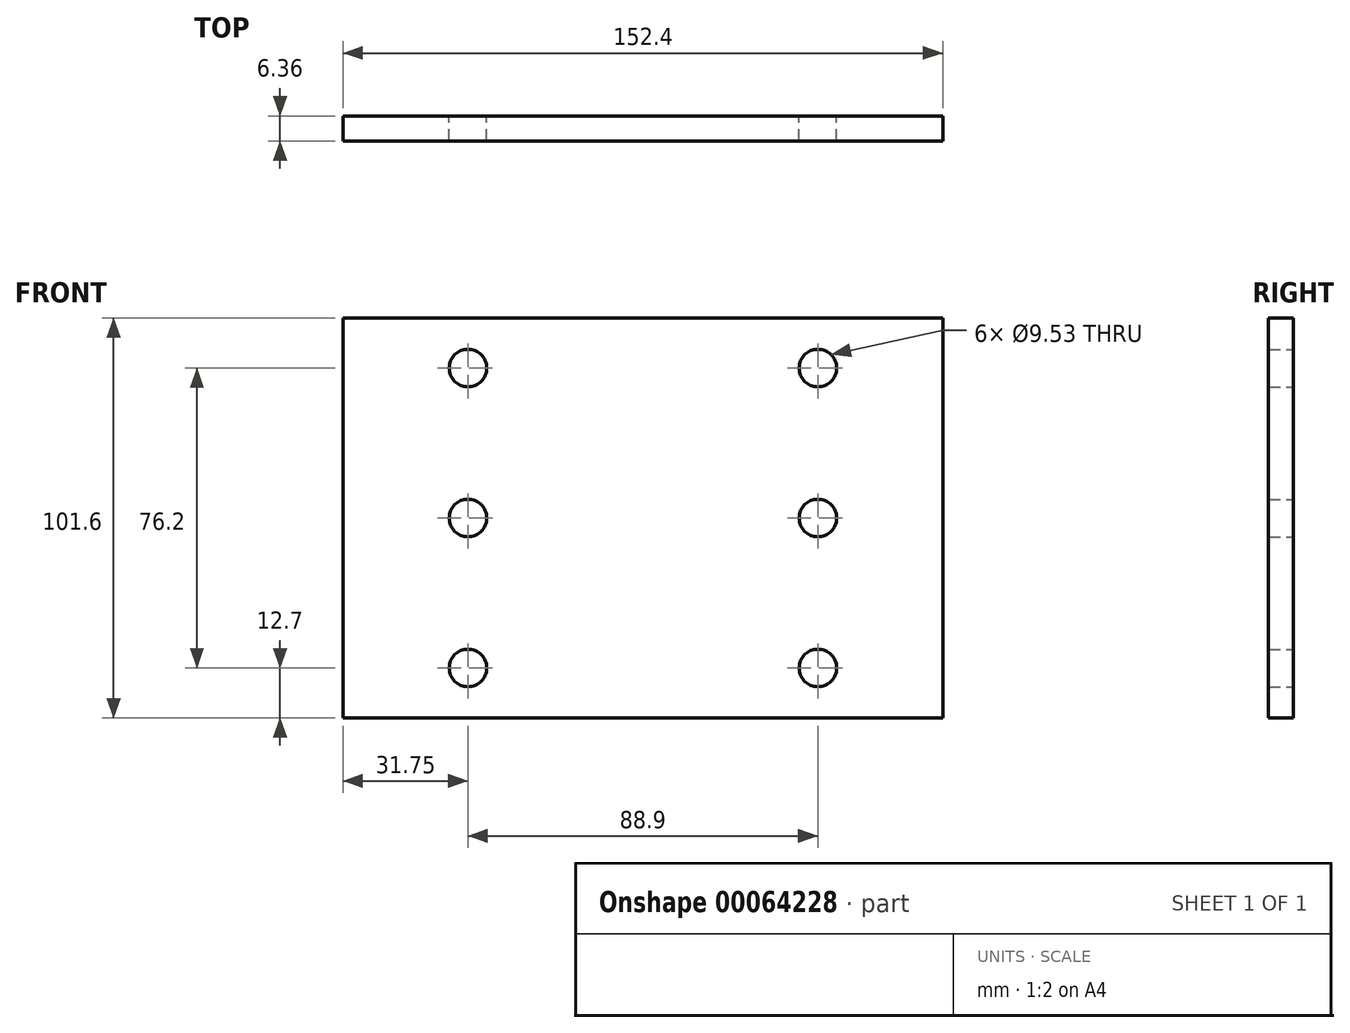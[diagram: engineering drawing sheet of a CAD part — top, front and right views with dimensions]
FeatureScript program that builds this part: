
annotation { "Feature Type Name" : "Feature", "Feature Type Description" : "" }
export const myFeature = defineFeature(function(context is Context, id is Id, definition is map)
    precondition{}
    {
        {
            var Q0;
            Q0=qCreatedBy(makeId("Front.planeOp"),FACE);
            var sketch = newSketch(context, id + "F0", { "sketchPlane" : qUnion([Q0])});
            skLineSegment(sketch, "E0.rect.bottom", {"start": v(76.2, 50.8) * mm, "end": v(-76.2, 50.8) * mm});
            skLineSegment(sketch, "E0.rect.top", {"start": v(76.2, -50.8) * mm, "end": v(-76.2, -50.8) * mm});
            skLineSegment(sketch, "E0.rect.left", {"start": v(76.2, 50.8) * mm, "end": v(76.2, -50.8) * mm});
            skLineSegment(sketch, "E0.rect.right", {"start": v(-76.2, 50.8) * mm, "end": v(-76.2, -50.8) * mm});
            skCircle(sketch, "E1", {"center": v(-44.45, 38.1) * mm, "radius": 4.76 * mm});
            skCircle(sketch, "E2.0.1.0", {"center": v(-44.45, 0) * mm, "radius": 4.76 * mm});
            skCircle(sketch, "E2.0.2.0", {"center": v(-44.45, -38.1) * mm, "radius": 4.76 * mm});
            skCircle(sketch, "E2.1.0.0", {"center": v(44.45, 38.1) * mm, "radius": 4.76 * mm});
            skCircle(sketch, "E2.1.1.0", {"center": v(44.45, 0) * mm, "radius": 4.76 * mm});
            skCircle(sketch, "E2.1.2.0", {"center": v(44.45, -38.1) * mm, "radius": 4.76 * mm});
            skLineSegment(sketch, "E2.direction1", {"start": v(-44.45, 38.1) * mm, "end": v(44.45, 38.1) * mm, "construction": true});
            skLineSegment(sketch, "E2.direction2", {"start": v(-44.45, 38.1) * mm, "end": v(-44.45, 0) * mm, "construction": true});
            skSolve(sketch);
        }
        {
            var Q0;
            Q0 = qSketchRegion(id + "F0", true);
            extrude(context, id + "F1", {"entities" : qUnion([Q0]), "endBound" : BoundingType.SYMMETRIC, "depth" : 6.35 * mm});
        }
    });
